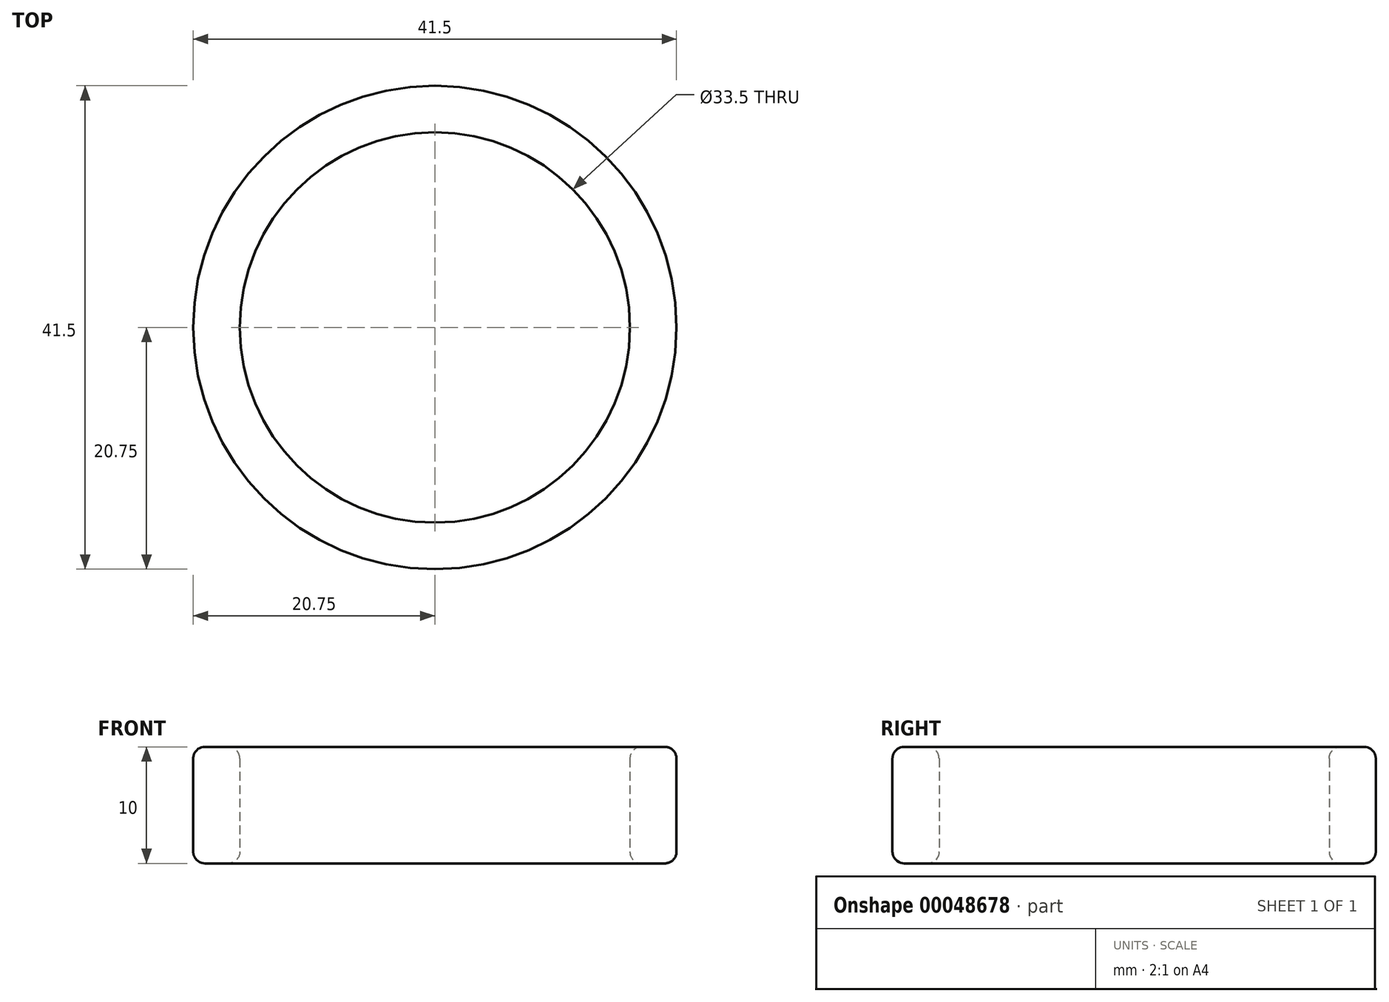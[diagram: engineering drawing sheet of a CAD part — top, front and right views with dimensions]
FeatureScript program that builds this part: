
annotation { "Feature Type Name" : "Feature", "Feature Type Description" : "" }
export const myFeature = defineFeature(function(context is Context, id is Id, definition is map)
    precondition{}
    {
        {
            var Q0;
            Q0=qCreatedBy(makeId("Top.planeOp"),FACE);
            var sketch = newSketch(context, id + "F0", { "sketchPlane" : qUnion([Q0])});
            skCircle(sketch, "E0", {"center": v(0, 0) * mm, "radius": 16.75 * mm});
            skCircle(sketch, "E1", {"center": v(0, 0) * mm, "radius": 20.75 * mm});
            skSolve(sketch);
        }
        {
            var Q0;
            Q0=makeQuery(id+"F0.imprint","IMPRINT",FACE,{"disambiguationData":[TD([[makeQuery(id+"F0.imprint","IMPRINT",EDGE,{"derivedFrom":sQuery(id+"F0.wireOp",EDGE,"E0")}),-1.0]])]});
            extrude(context, id + "F1", {"entities" : qUnion([Q0]), "depth" : 10 * mm});
        }
        {
            var Q0;
            Q0=makeQuery(id+"F1.opExtrude","CAP_EDGE",EDGE,{"disambiguationData":[OSD([sQuery(id+"F0.wireOp",EDGE,"E1")])],"isStart":false});
            var Q1;
            Q1=makeQuery(id+"F1.opExtrude","CAP_EDGE",EDGE,{"disambiguationData":[OSD([sQuery(id+"F0.wireOp",EDGE,"E0")])],"isStart":false});
            var Q2;
            Q2=makeQuery(id+"F1.opExtrude","CAP_EDGE",EDGE,{"disambiguationData":[OSD([sQuery(id+"F0.wireOp",EDGE,"E1")])],"isStart":true});
            var Q3;
            Q3=makeQuery(id+"F1.opExtrude","CAP_EDGE",EDGE,{"disambiguationData":[OSD([sQuery(id+"F0.wireOp",EDGE,"E0")])],"isStart":true});
            fillet(context, id + "F2", {"entities" : qUnion([Q0, Q1, Q2, Q3]), "radius" : 1 * mm, "tangentPropagation" : true, "allowEdgeOverflow" : false});
        }
    });
